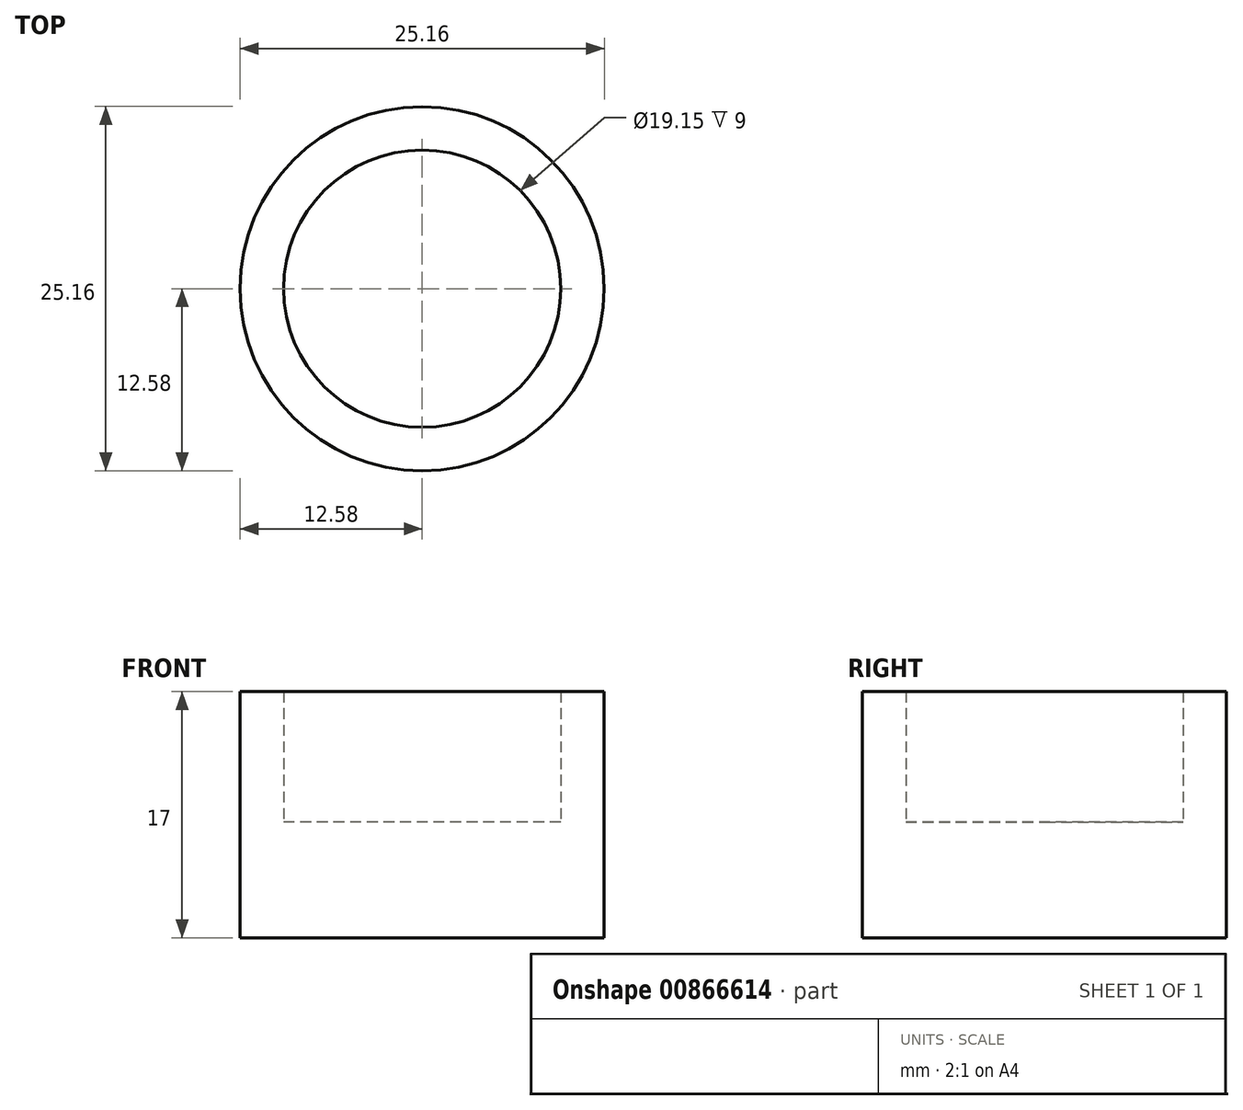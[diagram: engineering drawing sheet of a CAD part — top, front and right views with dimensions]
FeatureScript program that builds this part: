
annotation { "Feature Type Name" : "Feature", "Feature Type Description" : "" }
export const myFeature = defineFeature(function(context is Context, id is Id, definition is map)
    precondition{}
    {
        {
            var Q0;
            Q0=qCreatedBy(makeId("Top.planeOp"),FACE);
            var sketch = newSketch(context, id + "F0", { "sketchPlane" : qUnion([Q0])});
            skCircle(sketch, "E0", {"center": v(0, 0) * mm, "radius": 9.57 * mm});
            skSolve(sketch);
        }
        {
            var Q0;
            Q0 = qSketchRegion(id + "F0", true);
            extrude(context, id + "F1", {"entities" : qUnion([Q0]), "depth" : 9 * mm, "offsetDistance" : 25 * mm});
        }
        {
            var Q0;
            Q0=makeQuery(id+"F1.opExtrude","CAP_FACE",FACE,{"disambiguationData":[OSD([sQuery(id+"F0.wireOp",EDGE,"E0")])],"isStart":false});
            var Q1;
            Q1=makeQuery(id+"F1.opExtrude","SWEPT_BODY",BODY,{"disambiguationData":[OSD([sQuery(id+"F0.wireOp",EDGE,"E0")])]});
            shell(context, id + "F2", {"entities" : qUnion([Q0]), "parts" : qUnion([Q1]), "thickness" : 3 * mm, "oppositeDirection" : true});
        }
        {
            var Q0;
            Q0=makeQuery(id+"F1.opExtrude","CAP_FACE",FACE,{"disambiguationData":[OSD([sQuery(id+"F0.wireOp",EDGE,"E0")])],"isStart":true});
            extrude(context, id + "F3", {"entities" : qUnion([Q0]), "operationType" : NewBodyOperationType.ADD, "depth" : 5 * mm, "offsetDistance" : 25 * mm});
        }
    });
